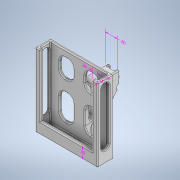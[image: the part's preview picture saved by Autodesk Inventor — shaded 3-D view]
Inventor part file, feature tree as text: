
AUTODESK INVENTOR PART (.ipt)
format: ipt  version: 2020.2 (Build 242310000, 310)  size: 901,120 bytes
history: native  units: in
note: dims shown in document units (in); Inventor stores cm internally (conversion verified against a paired STEP export)
features: sketch x11, extrude x9, chamfer x7, other x5, fillet x5, hole x2
ambient origin geometry x8: Origin, YZ Plane, XZ Plane, XY Plane, X Axis, Y Axis, Z Axis, Center Point
bodies: Solid1 (feature_tree)
feature tree (39):
  other  "Annotations"
  extrude  "Extrusion1"  Depth=0.8in
  extrude  "Extrusion2"  Depth=0.15in
  extrude  "Extrusion3"  Depth=0.15in
  extrude  "Extrusion4"  Depth=3.6in TaperAngle=0.0deg
  extrude  "Extrusion5"  Depth=0.42in
  extrude  "Extrusion6"  Depth=0.28in
  chamfer  "Chamfer1"  Distance=0.15in
  extrude  "Extrusion7"  Depth=0.59in
  sketch  "Sketch9"  dims[d26=0.2in d27=0.2in]
  sketch  "Sketch10"  dims[d28=4.0in d29=0.0in d30=0.3in]
  extrude  "Extrusion8"  Depth=0.2in
  extrude  "Extrusion9"  Depth=0.3in
  chamfer  "Chamfer2"  Distance=0.7in
  chamfer  "Chamfer3"  Distance=0.7in
  chamfer  "Chamfer4"  Distance=0.35in
  chamfer  "Chamfer5"  Distance=1.0in
  chamfer  "Chamfer6"  Distance=1.5in
  chamfer  "Chamfer7"  Distance=1.8in Angle=45.0deg
  fillet  "Fillet1"  Radius=0.3in
  fillet  "Fillet2"  Radius=0.3in
  fillet  "Fillet3"  Radius=1.0in
  fillet  "Fillet4"  Radius=0.125in
  fillet  "Fillet5"  Radius=0.125in
  hole  "Hole1"  [1 undecoded]
  hole  "Hole2"  [1 undecoded]
  sketch  "Sketch1"  dims[d0=3.2in d1=0.8in]
  sketch  "Sketch2"  dims[d2=0.17in d3=0.0in d4=0.15in]
  sketch  "Sketch4"  dims[d5=0.15in d6=0.15in]
  sketch  "Sketch5"  dims[d7=0.15in d8=3.6in d9=0.0in]
  sketch  "Sketch6"  dims[d10=0.17in d11=0.42in]
  sketch  "Sketch7"  dims[d12=0.28in d13=0.28in d14=0.15in d15=0.0in]
  sketch  "Sketch8"  dims[d24=0.2in d25=0.59in]
  sketch  "Sketch11"  dims[d31=0.6in]
  sketch  "Sketch12"  dims[d32=0.6in d34=0.7in d35=0.7in d36=0.35in d37=1.0in d38=0.0in d39=1.5in d40=0.0in d41=1.8in d42=1.5in d43=45.0deg d44=0.3in d45=0.3in d46=1.0in d47=0.0in d51=0.125in d52=0.125in d53=0.125in d54=0.125in d55=0.13in d56=0.0in d57=0.13in d58=0.0in d59=0.2in d60=0.13in d61=45.0deg d62=0.2in d63=0.13in d64=45.0deg d65=0.1in d66=0.13in d67=45.0deg d68=0.1in d69=0.13in d70=45.0deg d71=0.1in d72=0.13in d73=45.0deg d74=0.1in d75=0.13in d76=45.0deg d77=0.2in d78=0.3in d79=0.05in d80=0.05in d81=0.04in d82=0.061in d83=0.061in d84=0.12in d85=0.75in d86=0.119in d87=0.25in d88=0.5635in d89=0.3in d90=0.8108in d91=0.061in d92=0.3in d93=0.061in d94=0.061in d95=0.3in d96=0.061in d97=0.3in d98=0.12in d99=0.75in d100=0.119in d101=0.25in d102=0.5635in d103=0.3in d104=0.8108in d16=0.1873in d17=0.2224in d18=0.59in d19=0.3645in d20=0.0277in d21=0.28in d22=0.1162in d23=0.15in d48=0.1879in d49=0.1703in d50=0.6in]
  other  "Linear Dimension 1"
  other  "Linear Dimension 2"
  other  "Linear Dimension 3"
  other  "Linear Dimension 4"
note: 2 required parameter values undecoded (feature->parameter linkage not recoverable at this tier; creation-order binding heuristic only, values carry confidence <= 0.55)
